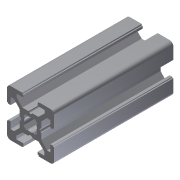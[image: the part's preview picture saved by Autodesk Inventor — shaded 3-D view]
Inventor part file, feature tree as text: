
AUTODESK INVENTOR PART (.ipt)
format: ipt  version: 2011 (Build 150239000, 239)  size: 176,640 bytes
history: native  units: in
note: dims shown in document units (in); Inventor stores cm internally (conversion verified against a paired STEP export)
features: extrude x1, sketch x1
ambient origin geometry x8: Origin, YZ Plane, XZ Plane, XY Plane, X Axis, Y Axis, Z Axis, Center Point
bodies: Solid1 (feature_tree)
feature tree (2):
  extrude  "Extrusion1"  [1 undecoded]
  sketch  "Sketch1"  dims[d0=2.0in d1=0.0in]
note: 1 required parameter value undecoded (feature->parameter linkage not recoverable at this tier; creation-order binding heuristic only, values carry confidence <= 0.55)
